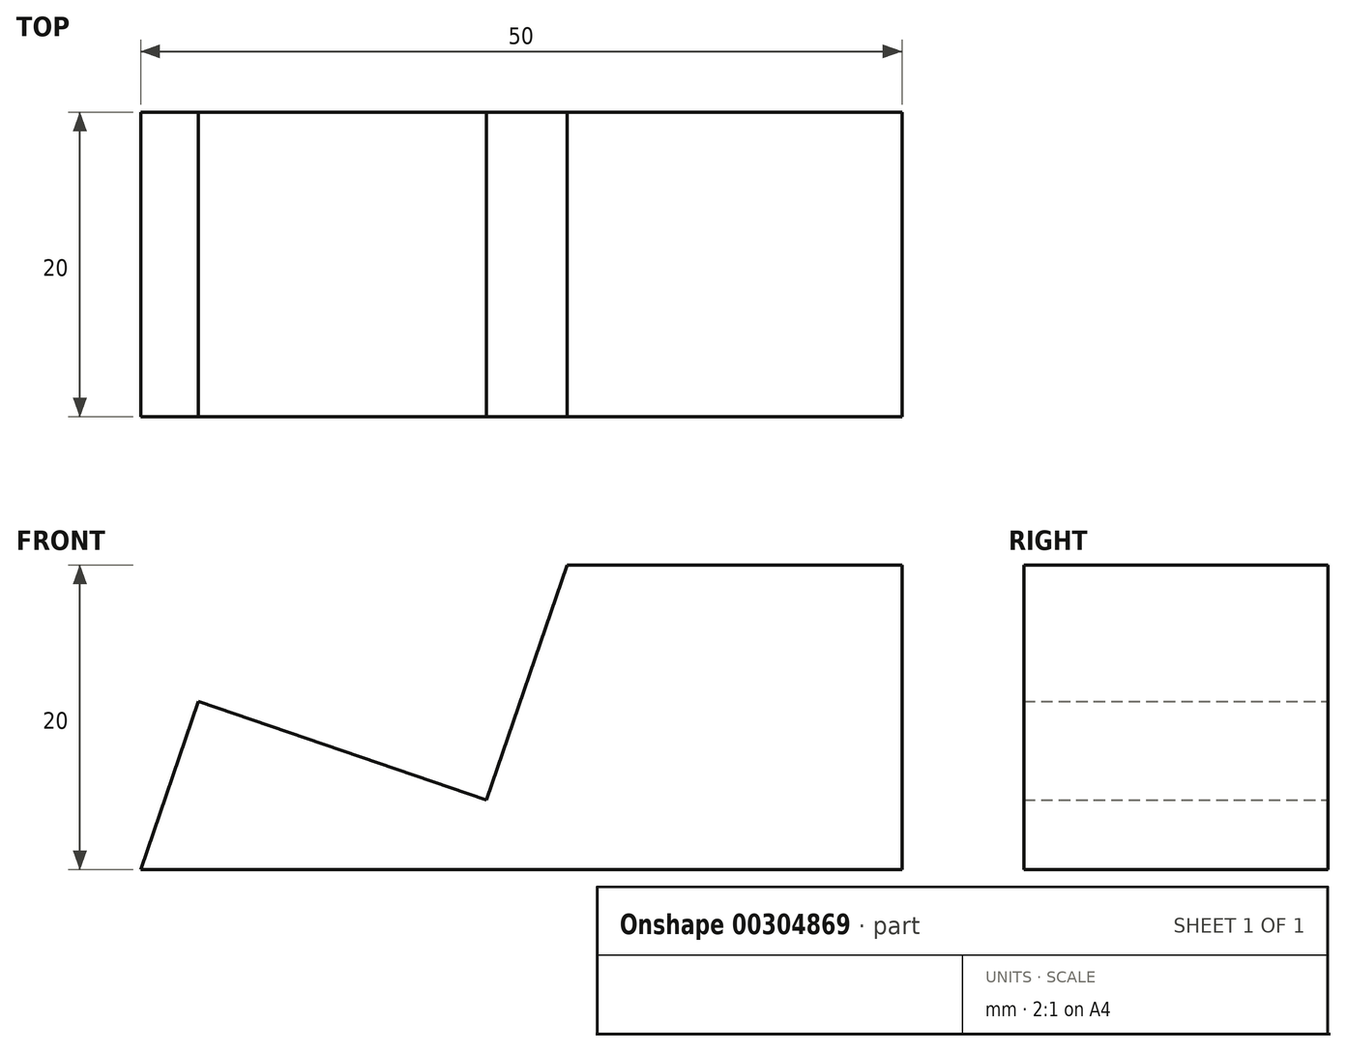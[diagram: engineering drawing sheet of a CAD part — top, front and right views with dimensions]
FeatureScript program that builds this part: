
annotation { "Feature Type Name" : "Feature", "Feature Type Description" : "" }
export const myFeature = defineFeature(function(context is Context, id is Id, definition is map)
    precondition{}
    {
        {
            var Q0;
            Q0=qCreatedBy(makeId("Front.planeOp"),FACE);
            var sketch = newSketch(context, id + "F0", { "sketchPlane" : qUnion([Q0])});
            skLineSegment(sketch, "E0", {"start": v(-50, 0) * mm, "end": v(0, 0) * mm});
            skLineSegment(sketch, "E1", {"start": v(0, 0) * mm, "end": v(0, 20) * mm});
            skLineSegment(sketch, "E2", {"start": v(0, 20) * mm, "end": v(-22, 20) * mm});
            skLineSegment(sketch, "E3", {"start": v(-22, 20) * mm, "end": v(-27.29, 4.57) * mm});
            skLineSegment(sketch, "E4", {"start": v(-27.29, 4.57) * mm, "end": v(-46.2, 11.06) * mm});
            skLineSegment(sketch, "E5", {"start": v(-46.2, 11.06) * mm, "end": v(-50, 0) * mm});
            skLineSegment(sketch, "E6", {"start": v(-22, 20) * mm, "end": v(70, 288.36) * mm, "construction": true});
            skLineSegment(sketch, "E7", {"start": v(70, 288.36) * mm, "end": v(70, 0) * mm, "construction": true});
            skLineSegment(sketch, "E8", {"start": v(70, 0) * mm, "end": v(0, 0) * mm, "construction": true});
            skSolve(sketch);
        }
        {
            var Q0;
            Q0 = qSketchRegion(id + "F0", true);
            extrude(context, id + "F1", {"entities" : qUnion([Q0]), "depth" : 20 * mm});
        }
    });
